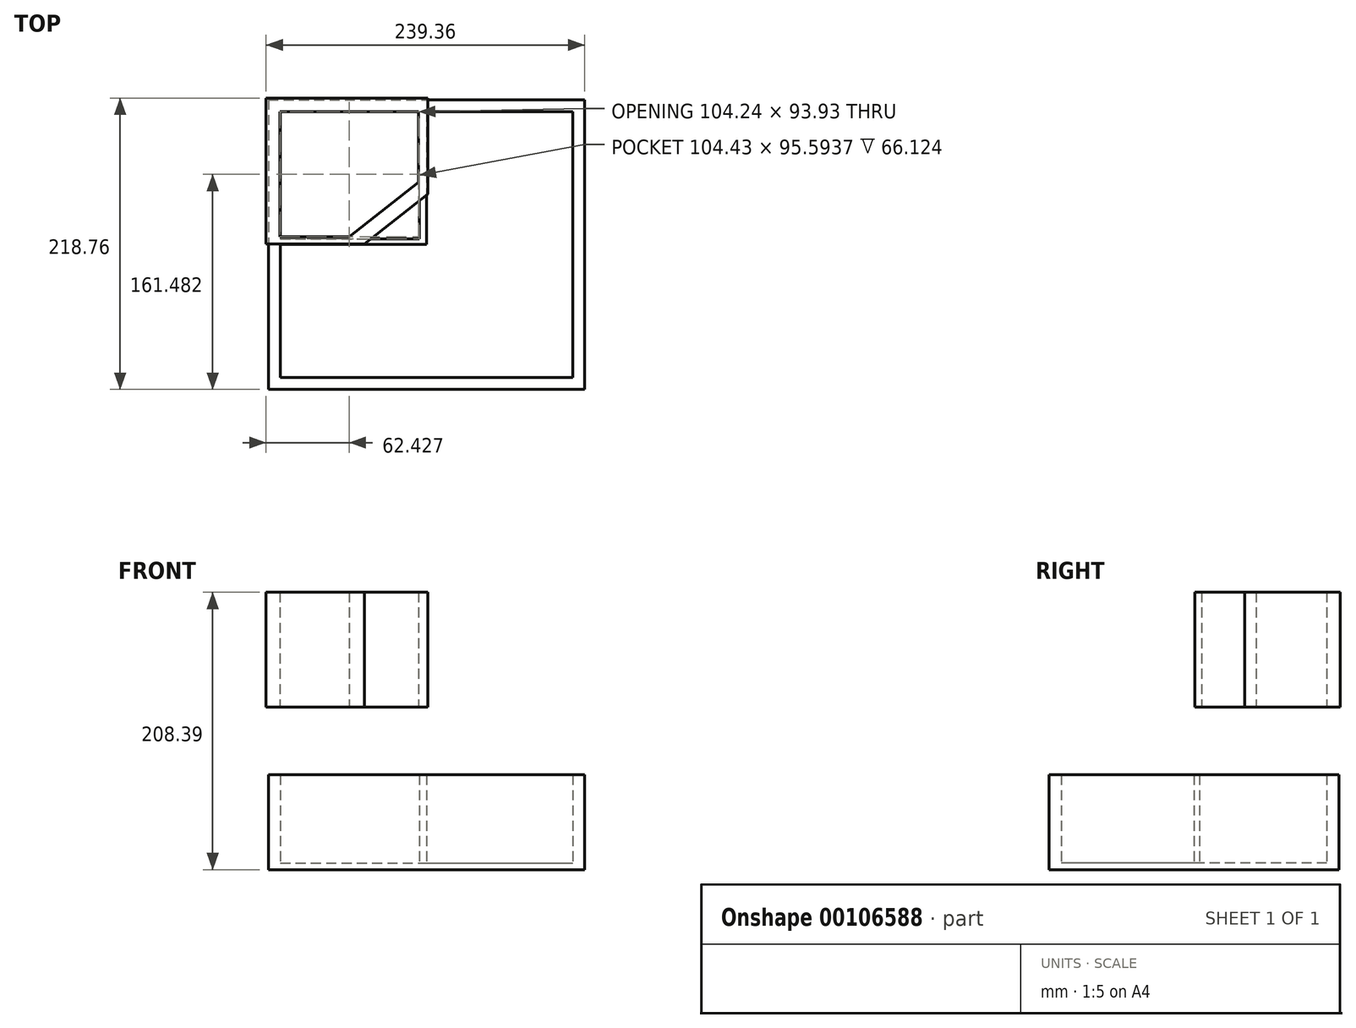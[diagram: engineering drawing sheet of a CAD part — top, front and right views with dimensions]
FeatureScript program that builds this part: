
annotation { "Feature Type Name" : "Feature", "Feature Type Description" : "" }
export const myFeature = defineFeature(function(context is Context, id is Id, definition is map)
    precondition{}
    {
        {
            var Q0;
            Q0=qCreatedBy(makeId("Top.planeOp"),FACE);
            var sketch = newSketch(context, id + "F0", { "sketchPlane" : qUnion([Q0])});
            skLineSegment(sketch, "E0.bottom", {"start": v(-118.8, 108.79) * mm, "end": v(118.8, 108.79) * mm});
            skLineSegment(sketch, "E0.top", {"start": v(-118.8, -108.79) * mm, "end": v(118.8, -108.79) * mm});
            skLineSegment(sketch, "E0.left", {"start": v(-118.8, 108.79) * mm, "end": v(-118.8, -108.79) * mm});
            skLineSegment(sketch, "E0.right", {"start": v(118.8, 108.79) * mm, "end": v(118.8, -108.79) * mm});
            skPoint(sketch, "E0.middle", {"position": v(0, 0) * mm});
            skLineSegment(sketch, "E1.0", {"start": v(-109.84, 99.82) * mm, "end": v(-5.4, 99.82) * mm});
            skLineSegment(sketch, "E1.1", {"start": v(-109.84, 99.82) * mm, "end": v(-109.84, 4.23) * mm});
            skLineSegment(sketch, "E1.2", {"start": v(-109.84, -99.82) * mm, "end": v(109.84, -99.82) * mm});
            skLineSegment(sketch, "E1.3", {"start": v(109.84, 99.82) * mm, "end": v(109.84, -99.82) * mm});
            skLineSegment(sketch, "E2.bottom", {"start": v(-109.84, 4.23) * mm, "end": v(-5.4, 4.23) * mm});
            skLineSegment(sketch, "E2.top", {"start": v(-109.84, 0) * mm, "end": v(0, 0) * mm});
            skLineSegment(sketch, "E2.right", {"start": v(0, 4.23) * mm, "end": v(0, 0) * mm});
            skLineSegment(sketch, "E3.left", {"start": v(0, 4.23) * mm, "end": v(0, 99.82) * mm});
            skLineSegment(sketch, "E3.right", {"start": v(-5.4, 4.23) * mm, "end": v(-5.4, 99.82) * mm});
            skLineSegment(sketch, "E4.trimOffspring", {"start": v(0, 99.82) * mm, "end": v(109.84, 99.82) * mm});
            skLineSegment(sketch, "E5.trimOffspring", {"start": v(-109.84, 0) * mm, "end": v(-109.84, -99.82) * mm});
            skSolve(sketch);
        }
        {
            var Q0;
            Q0=makeQuery(id+"F0.imprint","IMPRINT",FACE,{"disambiguationData":[TD([[makeQuery(id+"F0.imprint","IMPRINT",EDGE,{"derivedFrom":sQuery(id+"F0.wireOp",EDGE,"E0.bottom")}),-1.0]])]});
            var Q1;
            Q1 = qConstructionFilter(qBodyType(qCreatedBy(id + "F0" ,EDGE), BodyType.WIRE), ConstructionObject.NO);
            extrude(context, id + "F1", {"entities" : qUnion([Q0]), "surfaceEntities" : qUnion([Q1]), "depth" : 66.12 * mm});
        }
        {
            var Q0;
            Q0=makeQuery(id+"F1.opExtrude","CAP_FACE",FACE,{"disambiguationData":[OSD([sQuery(id+"F0.wireOp",EDGE,"E0.bottom"),sQuery(id+"F0.wireOp",EDGE,"E0.top"),sQuery(id+"F0.wireOp",EDGE,"E0.left"),sQuery(id+"F0.wireOp",EDGE,"E0.right"),sQuery(id+"F0.wireOp",EDGE,"E1.0"),sQuery(id+"F0.wireOp",EDGE,"E1.1"),sQuery(id+"F0.wireOp",EDGE,"E1.2"),sQuery(id+"F0.wireOp",EDGE,"E1.3"),sQuery(id+"F0.wireOp",EDGE,"E2.bottom"),sQuery(id+"F0.wireOp",EDGE,"E2.top"),sQuery(id+"F0.wireOp",EDGE,"E2.right"),sQuery(id+"F0.wireOp",EDGE,"E3.left"),sQuery(id+"F0.wireOp",EDGE,"E3.right"),sQuery(id+"F0.wireOp",EDGE,"E4.trimOffspring"),sQuery(id+"F0.wireOp",EDGE,"E5.trimOffspring")])],"isStart":true});
            var sketch = newSketch(context, id + "F2", { "sketchPlane" : qUnion([Q0])});
            skLineSegment(sketch, "E6.bottom", {"start": v(118.8, 108.79) * mm, "end": v(-118.8, 108.79) * mm});
            skLineSegment(sketch, "E6.top", {"start": v(118.8, -108.79) * mm, "end": v(-118.8, -108.79) * mm});
            skLineSegment(sketch, "E6.left", {"start": v(118.8, 108.79) * mm, "end": v(118.8, -108.79) * mm});
            skLineSegment(sketch, "E6.right", {"start": v(-118.8, 108.79) * mm, "end": v(-118.8, -108.79) * mm});
            skSolve(sketch);
        }
        {
            var Q0;
            Q0 = qSketchRegion(id + "F2", true);
            extrude(context, id + "F3", {"entities" : qUnion([Q0]), "operationType" : NewBodyOperationType.ADD, "depth" : 5.08 * mm});
        }
        {
            var Q0;
            Q0=makeQuery(id+"F1.opExtrude","CAP_FACE",FACE,{"disambiguationData":[OSD([sQuery(id+"F0.wireOp",EDGE,"E0.bottom"),sQuery(id+"F0.wireOp",EDGE,"E0.top"),sQuery(id+"F0.wireOp",EDGE,"E0.left"),sQuery(id+"F0.wireOp",EDGE,"E0.right"),sQuery(id+"F0.wireOp",EDGE,"E1.0"),sQuery(id+"F0.wireOp",EDGE,"E1.1"),sQuery(id+"F0.wireOp",EDGE,"E1.2"),sQuery(id+"F0.wireOp",EDGE,"E1.3"),sQuery(id+"F0.wireOp",EDGE,"E2.bottom"),sQuery(id+"F0.wireOp",EDGE,"E2.top"),sQuery(id+"F0.wireOp",EDGE,"E2.right"),sQuery(id+"F0.wireOp",EDGE,"E3.left"),sQuery(id+"F0.wireOp",EDGE,"E3.right"),sQuery(id+"F0.wireOp",EDGE,"E4.trimOffspring"),sQuery(id+"F0.wireOp",EDGE,"E5.trimOffspring")])],"isStart":false});
            cPlane(context, id + "F4", {"entities" : qUnion([Q0]), "cplaneType" : CPlaneType.OFFSET, "offset" : 50.8 * mm, "width" : 152.4 * mm, "height" : 152.4 * mm});
        }
        {
            var Q0;
            Q0=qCreatedBy(id+"F4.planeOp",FACE);
            var sketch = newSketch(context, id + "F5", { "sketchPlane" : qUnion([Q0])});
            skLineSegment(sketch, "E7.bottom", {"start": v(-120.56, 109.97) * mm, "end": v(0.86, 109.97) * mm});
            skLineSegment(sketch, "E7.top", {"start": v(-120.56, 0.57) * mm, "end": v(-46.7, 0.57) * mm});
            skLineSegment(sketch, "E7.left", {"start": v(-120.56, 109.97) * mm, "end": v(-120.56, 0.57) * mm});
            skLineSegment(sketch, "E7.right", {"start": v(0.86, 109.97) * mm, "end": v(0.86, 37.99) * mm});
            skLineSegment(sketch, "E8.bottom", {"start": v(-110.25, 99.66) * mm, "end": v(-6.01, 99.66) * mm});
            skLineSegment(sketch, "E8.top", {"start": v(-110.25, 5.73) * mm, "end": v(-58.13, 5.73) * mm});
            skLineSegment(sketch, "E8.left", {"start": v(-110.25, 99.66) * mm, "end": v(-110.25, 5.73) * mm});
            skLineSegment(sketch, "E8.right", {"start": v(-6.01, 99.66) * mm, "end": v(-6.01, 46.73) * mm});
            skLineSegment(sketch, "E9", {"start": v(-58.13, 5.73) * mm, "end": v(-6.01, 46.73) * mm});
            skPoint(sketch, "E10.endSnap0", {"position": v(0.86, 55.27) * mm});
            skLineSegment(sketch, "E11", {"start": v(0.86, 37.99) * mm, "end": v(-46.7, 0.57) * mm});
            skPoint(sketch, "E11.endSnap0", {"position": v(-59.85, 0.57) * mm});
            skPoint(sketch, "E12.orphan", {"position": v(-6.01, 5.73) * mm});
            skPoint(sketch, "E13.orphan", {"position": v(0.86, 0.57) * mm});
            skSolve(sketch);
        }
        {
            var Q0;
            Q0 = qSketchRegion(id + "F5", true);
            extrude(context, id + "F6", {"entities" : qUnion([Q0]), "depth" : 86.39 * mm});
        }
    });
